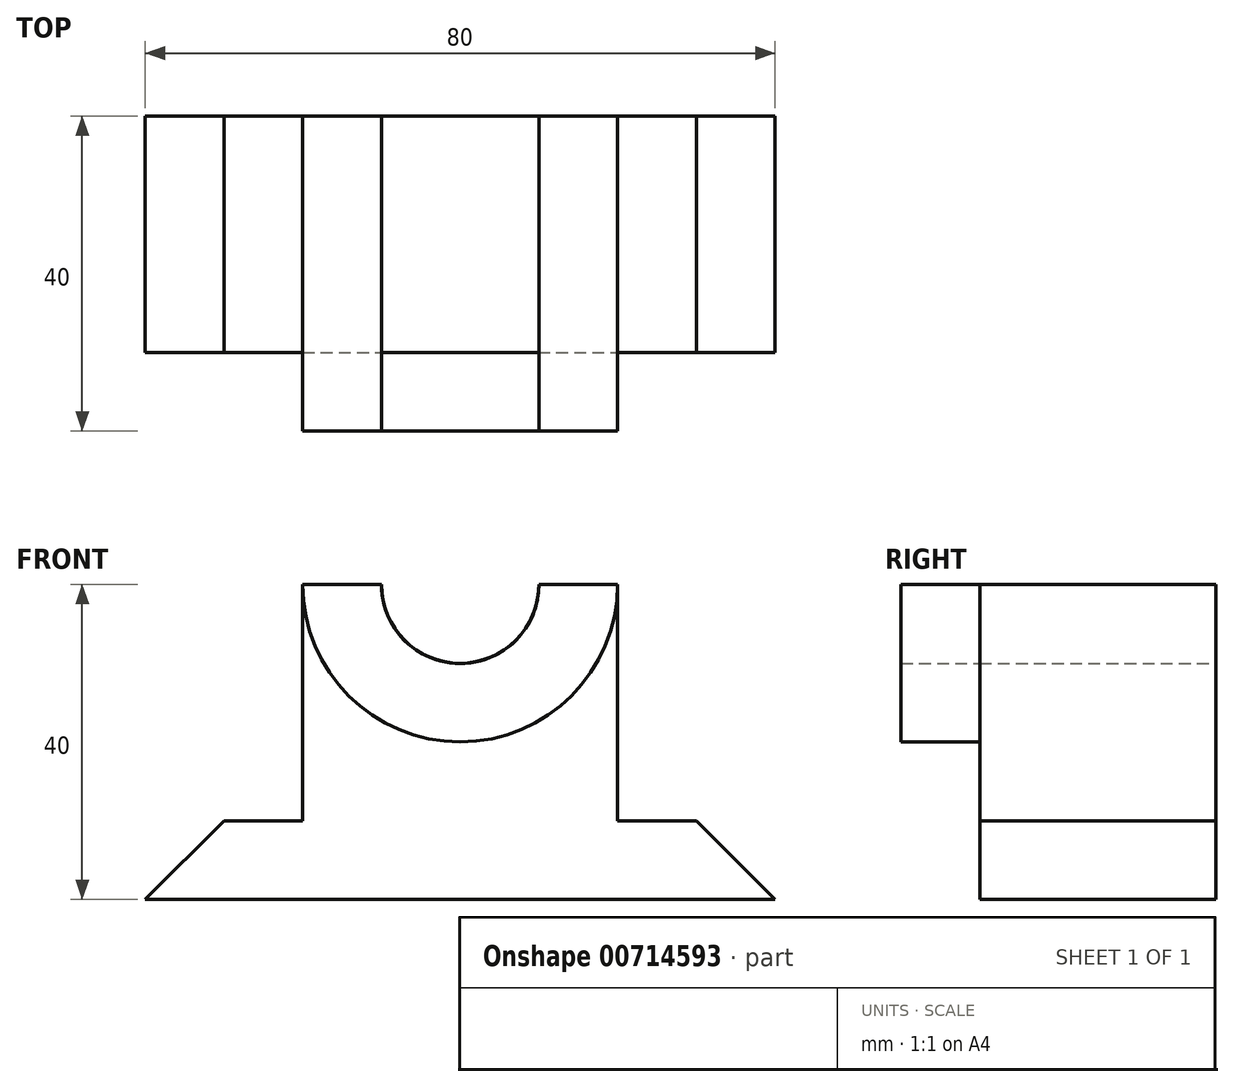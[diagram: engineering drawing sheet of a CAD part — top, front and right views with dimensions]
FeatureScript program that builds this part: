
annotation { "Feature Type Name" : "Feature", "Feature Type Description" : "" }
export const myFeature = defineFeature(function(context is Context, id is Id, definition is map)
    precondition{}
    {
        {
            var Q0;
            Q0=qCreatedBy(makeId("Front.planeOp"),FACE);
            var sketch = newSketch(context, id + "F0", { "sketchPlane" : qUnion([Q0])});
            skLineSegment(sketch, "E0", {"start": v(0, 0) * mm, "end": v(80, 0) * mm});
            skLineSegment(sketch, "E1", {"start": v(20, 10) * mm, "end": v(20, 40) * mm});
            skLineSegment(sketch, "E2", {"start": v(20, 40) * mm, "end": v(30, 40) * mm});
            skLineSegment(sketch, "E3", {"start": v(60, 10) * mm, "end": v(60, 40) * mm});
            skLineSegment(sketch, "E4", {"start": v(60, 40) * mm, "end": v(50, 40) * mm});
            skArc(sketch, "E5", {"start": v(30, 40) * mm, "mid": v(40, 30) * mm, "end": v(50, 40) * mm});
            skLineSegment(sketch, "E6", {"start": v(20, 10) * mm, "end": v(10, 10) * mm});
            skLineSegment(sketch, "E7", {"start": v(10, 10) * mm, "end": v(0, 0) * mm});
            skLineSegment(sketch, "E8", {"start": v(60, 10) * mm, "end": v(70, 10) * mm});
            skLineSegment(sketch, "E9", {"start": v(70, 10) * mm, "end": v(80, 0) * mm});
            skSolve(sketch);
        }
        {
            var Q0;
            Q0=makeQuery(id+"F0.imprint","IMPRINT",FACE,{"disambiguationData":[TD([[makeQuery(id+"F0.imprint","IMPRINT",EDGE,{"derivedFrom":sQuery(id+"F0.wireOp",EDGE,"E0")}),1.0]])]});
            extrude(context, id + "F1", {"entities" : qUnion([Q0]), "depth" : 30 * mm, "offsetDistance" : 25 * mm});
        }
        {
            var Q0;
            Q0=makeQuery(id+"F1.opExtrude","CAP_FACE",FACE,{"disambiguationData":[OSD([sQuery(id+"F0.wireOp",EDGE,"E0"),sQuery(id+"F0.wireOp",EDGE,"E1"),sQuery(id+"F0.wireOp",EDGE,"E2"),sQuery(id+"F0.wireOp",EDGE,"E3"),sQuery(id+"F0.wireOp",EDGE,"E4"),sQuery(id+"F0.wireOp",EDGE,"E5"),sQuery(id+"F0.wireOp",EDGE,"E6"),sQuery(id+"F0.wireOp",EDGE,"E7"),sQuery(id+"F0.wireOp",EDGE,"E8"),sQuery(id+"F0.wireOp",EDGE,"E9")])],"isStart":false});
            var sketch = newSketch(context, id + "F2", { "sketchPlane" : qUnion([Q0])});
            skArc(sketch, "E10", {"start": v(20, 40) * mm, "mid": v(40, 20) * mm, "end": v(60, 40) * mm});
            skLineSegment(sketch, "E11", {"start": v(20, 40) * mm, "end": v(30, 40) * mm});
            skArc(sketch, "E12", {"start": v(30, 40) * mm, "mid": v(40, 29.96) * mm, "end": v(50, 40) * mm});
            skLineSegment(sketch, "E13", {"start": v(60, 40) * mm, "end": v(50, 40) * mm});
            skSolve(sketch);
        }
        {
            var Q0;
            Q0=qSketchRegion(id+"F2",true);
            extrude(context, id + "F3", {"entities" : qUnion([Q0]), "operationType" : NewBodyOperationType.ADD, "depth" : 10 * mm, "offsetDistance" : 25 * mm});
        }
    });
